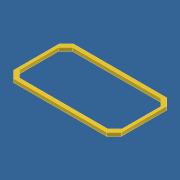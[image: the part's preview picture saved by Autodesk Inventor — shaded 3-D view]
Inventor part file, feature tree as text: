
AUTODESK INVENTOR PART (.ipt)
format: ipt  version: 2012 (Build 160160000, 160)  size: 113,664 bytes
history: native  units: mm
features: sketch x2, other x1, extrude x1
ambient origin geometry x8: Origin, YZ Plane, XZ Plane, XY Plane, X Axis, Y Axis, Z Axis, Center Point
feature tree (4):
  other  "Твердое тело1"
  sketch  "Эскиз1"
  sketch  "3D эскиз1"
  extrude  "Выдавливание2"  Depth=58.0mm
